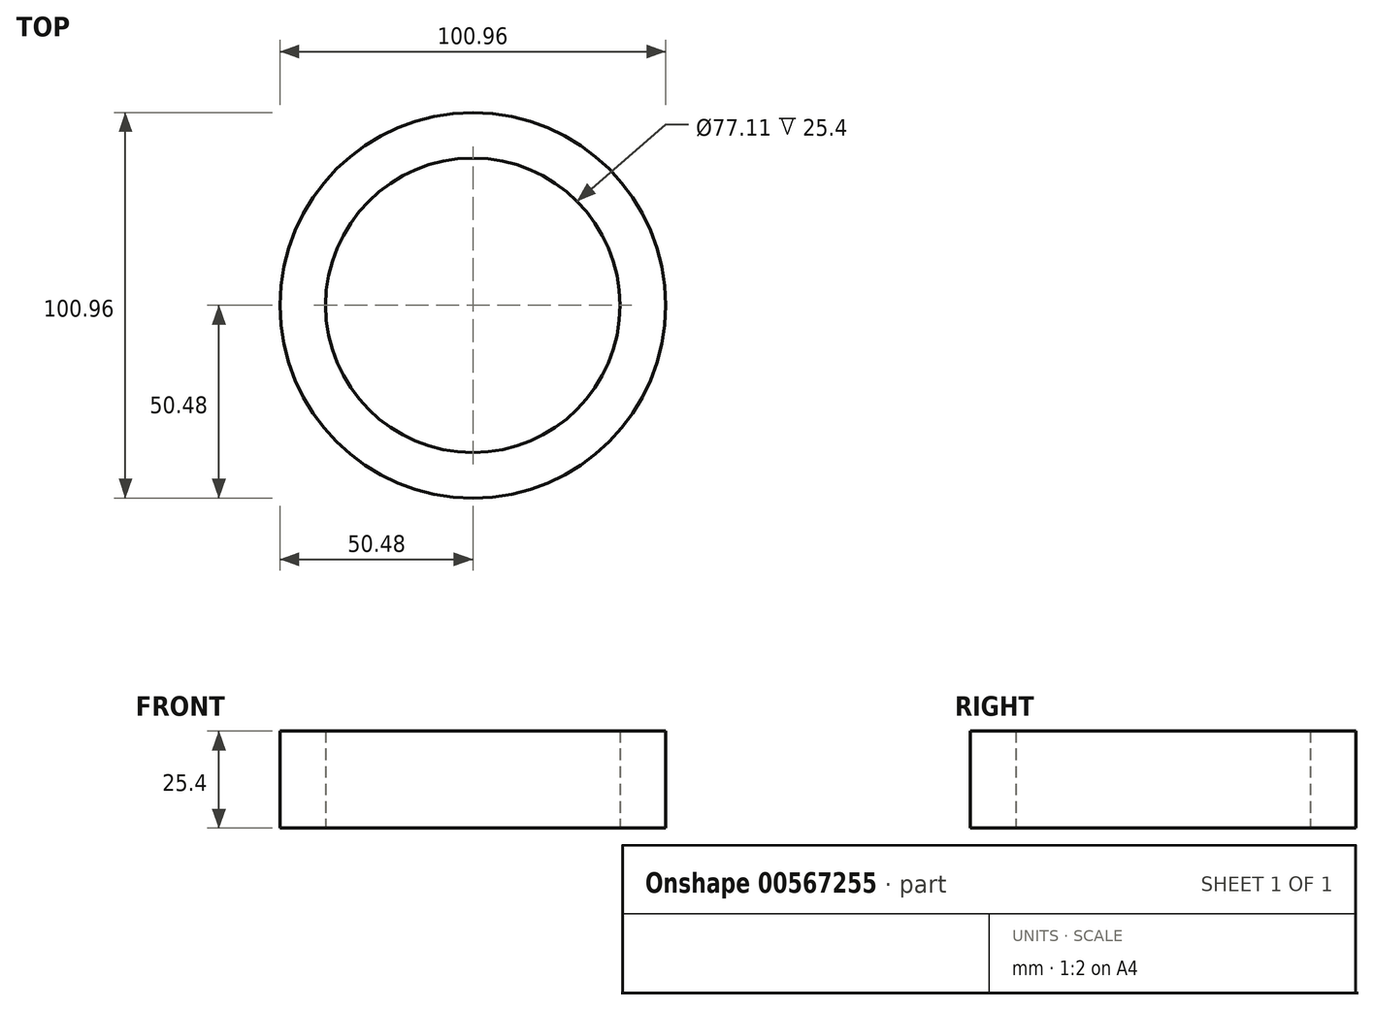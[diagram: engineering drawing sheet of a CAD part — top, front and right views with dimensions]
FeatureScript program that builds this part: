
annotation { "Feature Type Name" : "Feature", "Feature Type Description" : "" }
export const myFeature = defineFeature(function(context is Context, id is Id, definition is map)
    precondition{}
    {
        {
            var Q0;
            Q0=qCreatedBy(makeId("Top.planeOp"),FACE);
            var sketch = newSketch(context, id + "F0", { "sketchPlane" : qUnion([Q0])});
            skCircle(sketch, "E0", {"center": v(0, 0) * mm, "radius": 50.48 * mm});
            skCircle(sketch, "E1", {"center": v(0, 0) * mm, "radius": 38.56 * mm});
            skSolve(sketch);
        }
        {
            var Q0;
            Q0=qCreatedBy(makeId("Top.planeOp"),FACE);
            var sketch = newSketch(context, id + "F1", { "sketchPlane" : qUnion([Q0])});
            skSolve(sketch);
        }
        {
            var Q0;
            Q0 = qSketchRegion(id + "F1", true);
            var Q1;
            Q1 = qSketchRegion(id + "F0", true);
            extrude(context, id + "F2", {"entities" : qUnion([Q0, Q1]), "depth" : 25.4 * mm, "offsetDistance" : 25.4 * mm});
        }
    });
